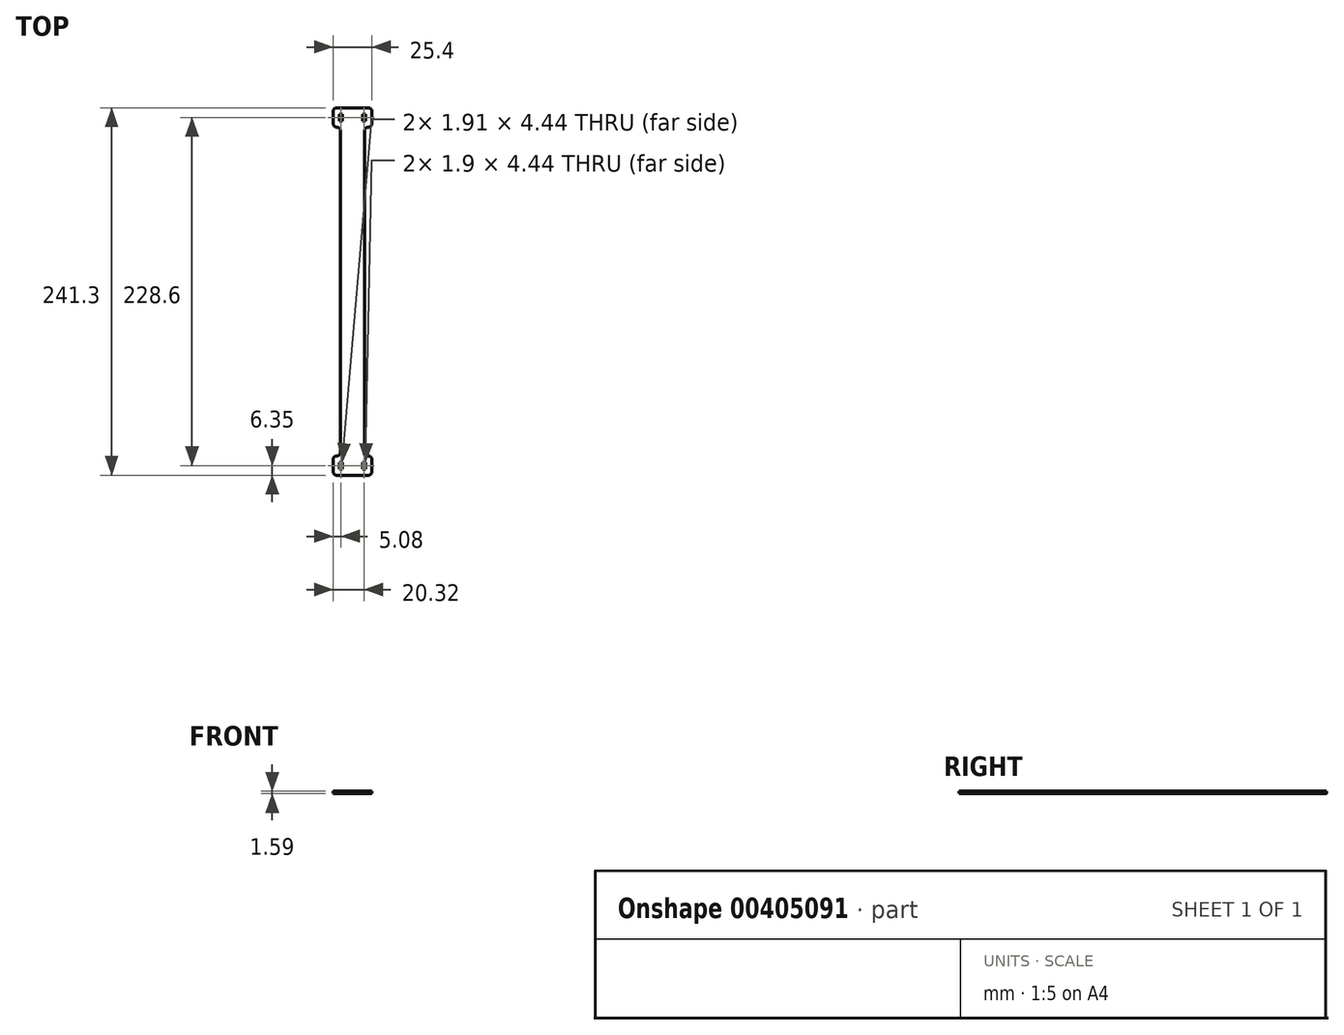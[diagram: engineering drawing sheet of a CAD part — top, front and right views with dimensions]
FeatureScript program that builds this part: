
annotation { "Feature Type Name" : "Feature", "Feature Type Description" : "" }
export const myFeature = defineFeature(function(context is Context, id is Id, definition is map)
    precondition{}
    {
        {
            var Q0;
            Q0=qCreatedBy(makeId("Top.planeOp"),FACE);
            var sketch = newSketch(context, id + "F0", { "sketchPlane" : qUnion([Q0])});
            skLineSegment(sketch, "E0.bottom", {"start": v(-101.6, 127) * mm, "end": v(101.6, 127) * mm, "construction": true});
            skLineSegment(sketch, "E0.top", {"start": v(-101.6, -127) * mm, "end": v(101.6, -127) * mm, "construction": true});
            skLineSegment(sketch, "E0.left", {"start": v(-101.6, 127) * mm, "end": v(-101.6, -127) * mm, "construction": true});
            skLineSegment(sketch, "E0.right", {"start": v(101.6, 127) * mm, "end": v(101.6, -127) * mm, "construction": true});
            skPoint(sketch, "E0.middle", {"position": v(0, 0) * mm});
            skLineSegment(sketch, "E1", {"start": v(-95.25, 120.65) * mm, "end": v(-69.85, 120.65) * mm});
            skLineSegment(sketch, "E2", {"start": v(-69.85, 120.65) * mm, "end": v(-69.85, 107.95) * mm});
            skLineSegment(sketch, "E3", {"start": v(-69.85, 107.95) * mm, "end": v(-74.61, 107.95) * mm});
            skLineSegment(sketch, "E4", {"start": v(-74.61, 107.95) * mm, "end": v(-74.61, -107.95) * mm});
            skLineSegment(sketch, "E5", {"start": v(-74.61, -107.95) * mm, "end": v(-69.85, -107.95) * mm});
            skLineSegment(sketch, "E6", {"start": v(-69.85, -107.95) * mm, "end": v(-69.85, -120.65) * mm});
            skLineSegment(sketch, "E7", {"start": v(-69.85, -120.65) * mm, "end": v(-95.25, -120.65) * mm});
            skLineSegment(sketch, "E8", {"start": v(-95.25, -120.65) * mm, "end": v(-95.25, -107.95) * mm});
            skLineSegment(sketch, "E9", {"start": v(-95.25, -107.95) * mm, "end": v(-90.49, -107.95) * mm});
            skLineSegment(sketch, "E10", {"start": v(-90.49, -107.95) * mm, "end": v(-90.49, 107.95) * mm});
            skLineSegment(sketch, "E11", {"start": v(-90.49, 107.95) * mm, "end": v(-95.25, 107.95) * mm});
            skLineSegment(sketch, "E12", {"start": v(-95.25, 107.95) * mm, "end": v(-95.25, 120.65) * mm});
            skLineSegment(sketch, "E13", {"start": v(-82.55, 120.65) * mm, "end": v(-82.55, -120.65) * mm, "construction": true});
            skLineSegment(sketch, "E14", {"start": v(-74.61, 0) * mm, "end": v(-90.49, 0) * mm, "construction": true});
            skPoint(sketch, "E15", {"position": v(-82.55, 0) * mm});
            skLineSegment(sketch, "E16.bottom", {"start": v(-91.12, 116.52) * mm, "end": v(-89.22, 116.52) * mm});
            skLineSegment(sketch, "E16.top", {"start": v(-91.12, 112.08) * mm, "end": v(-89.22, 112.08) * mm});
            skLineSegment(sketch, "E16.left", {"start": v(-91.12, 116.52) * mm, "end": v(-91.12, 112.08) * mm});
            skLineSegment(sketch, "E16.right", {"start": v(-89.22, 116.52) * mm, "end": v(-89.22, 112.08) * mm});
            skPoint(sketch, "E16.middle", {"position": v(-90.17, 114.3) * mm});
            skLineSegment(sketch, "E17", {"start": v(-95.25, 114.3) * mm, "end": v(-90.17, 114.3) * mm, "construction": true});
            skLineSegment(sketch, "E18.MirrorCS", {"start": v(-73.98, 116.52) * mm, "end": v(-75.88, 116.52) * mm});
            skLineSegment(sketch, "E19.MirrorCS", {"start": v(-73.98, 116.52) * mm, "end": v(-73.98, 112.08) * mm});
            skLineSegment(sketch, "E20.MirrorCS", {"start": v(-75.88, 116.52) * mm, "end": v(-75.88, 112.08) * mm});
            skLineSegment(sketch, "E21.MirrorCS", {"start": v(-73.98, 112.08) * mm, "end": v(-75.88, 112.08) * mm});
            skLineSegment(sketch, "E22.MirrorCS", {"start": v(-91.12, -116.52) * mm, "end": v(-89.22, -116.52) * mm});
            skLineSegment(sketch, "E23.MirrorCS", {"start": v(-91.12, -116.52) * mm, "end": v(-91.12, -112.08) * mm});
            skLineSegment(sketch, "E24.MirrorCS", {"start": v(-89.22, -116.52) * mm, "end": v(-89.22, -112.08) * mm});
            skLineSegment(sketch, "E25.MirrorCS", {"start": v(-91.12, -112.08) * mm, "end": v(-89.22, -112.08) * mm});
            skLineSegment(sketch, "E26.MirrorCS", {"start": v(-73.98, -116.52) * mm, "end": v(-75.88, -116.52) * mm});
            skLineSegment(sketch, "E27.MirrorCS", {"start": v(-75.88, -116.52) * mm, "end": v(-75.88, -112.08) * mm});
            skLineSegment(sketch, "E28.MirrorCS", {"start": v(-73.98, -112.08) * mm, "end": v(-75.88, -112.08) * mm});
            skLineSegment(sketch, "E29.MirrorCS", {"start": v(-73.98, -116.52) * mm, "end": v(-73.98, -112.08) * mm});
            skSolve(sketch);
        }
        {
            var Q0;
            Q0=makeQuery(id+"F0.imprint","IMPRINT",FACE,{"disambiguationData":[TD([[makeQuery(id+"F0.imprint","IMPRINT",EDGE,{"derivedFrom":sQuery(id+"F0.wireOp",EDGE,"E1")}),-1.0]])]});
            extrude(context, id + "F1", {"entities" : qUnion([Q0]), "depth" : 1.59 * mm, "offsetDistance" : 25.4 * mm});
        }
        {
            var Q0;
            Q0=makeQuery(id+"F1.opExtrude","SWEPT_EDGE",EDGE,{"disambiguationData":[OSD([sQuery(id+"F0.wireOp",EDGE,"E9"),sQuery(id+"F0.wireOp",EDGE,"E10")])]});
            var Q1;
            Q1=makeQuery(id+"F1.opExtrude","SWEPT_EDGE",EDGE,{"disambiguationData":[OSD([sQuery(id+"F0.wireOp",EDGE,"E8"),sQuery(id+"F0.wireOp",EDGE,"E9")])]});
            var Q2;
            Q2=makeQuery(id+"F1.opExtrude","SWEPT_EDGE",EDGE,{"disambiguationData":[OSD([sQuery(id+"F0.wireOp",EDGE,"E7"),sQuery(id+"F0.wireOp",EDGE,"E8")])]});
            var Q3;
            Q3=makeQuery(id+"F1.opExtrude","SWEPT_EDGE",EDGE,{"disambiguationData":[OSD([sQuery(id+"F0.wireOp",EDGE,"E6"),sQuery(id+"F0.wireOp",EDGE,"E7")])]});
            var Q4;
            Q4=makeQuery(id+"F1.opExtrude","SWEPT_EDGE",EDGE,{"disambiguationData":[OSD([sQuery(id+"F0.wireOp",EDGE,"E5"),sQuery(id+"F0.wireOp",EDGE,"E6")])]});
            var Q5;
            Q5=makeQuery(id+"F1.opExtrude","SWEPT_EDGE",EDGE,{"disambiguationData":[OSD([sQuery(id+"F0.wireOp",EDGE,"E4"),sQuery(id+"F0.wireOp",EDGE,"E5")])]});
            var Q6;
            Q6=makeQuery(id+"F1.opExtrude","SWEPT_EDGE",EDGE,{"disambiguationData":[OSD([sQuery(id+"F0.wireOp",EDGE,"E1"),sQuery(id+"F0.wireOp",EDGE,"E2")])]});
            var Q7;
            Q7=makeQuery(id+"F1.opExtrude","SWEPT_EDGE",EDGE,{"disambiguationData":[OSD([sQuery(id+"F0.wireOp",EDGE,"E2"),sQuery(id+"F0.wireOp",EDGE,"E3")])]});
            var Q8;
            Q8=makeQuery(id+"F1.opExtrude","SWEPT_EDGE",EDGE,{"disambiguationData":[OSD([sQuery(id+"F0.wireOp",EDGE,"E1"),sQuery(id+"F0.wireOp",EDGE,"E12")])]});
            var Q9;
            Q9=makeQuery(id+"F1.opExtrude","SWEPT_EDGE",EDGE,{"disambiguationData":[OSD([sQuery(id+"F0.wireOp",EDGE,"E11"),sQuery(id+"F0.wireOp",EDGE,"E12")])]});
            var Q10;
            Q10=makeQuery(id+"F1.opExtrude","SWEPT_EDGE",EDGE,{"disambiguationData":[OSD([sQuery(id+"F0.wireOp",EDGE,"E3"),sQuery(id+"F0.wireOp",EDGE,"E4")])]});
            var Q11;
            Q11=makeQuery(id+"F1.opExtrude","SWEPT_EDGE",EDGE,{"disambiguationData":[OSD([sQuery(id+"F0.wireOp",EDGE,"E10"),sQuery(id+"F0.wireOp",EDGE,"E11")])]});
            fillet(context, id + "F2", {"entities" : qUnion([Q0, Q1, Q2, Q3, Q4, Q5, Q6, Q7, Q8, Q9, Q10, Q11]), "radius" : 2.38 * mm, "tangentPropagation" : true, "allowEdgeOverflow" : false});
        }
    });
